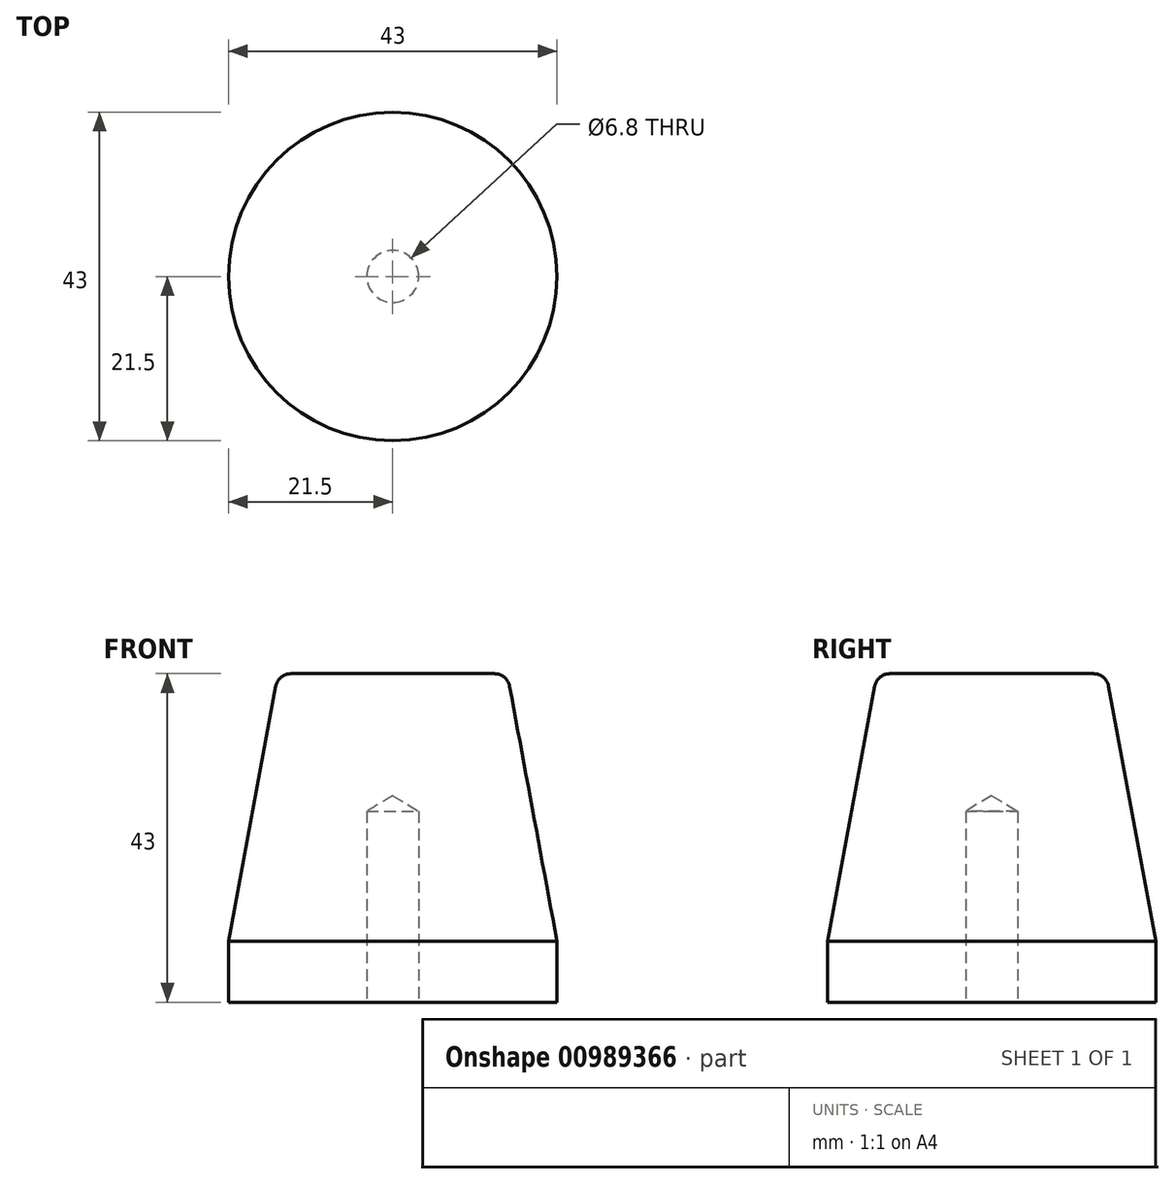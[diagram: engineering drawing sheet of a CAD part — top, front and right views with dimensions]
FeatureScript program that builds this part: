
annotation { "Feature Type Name" : "Feature", "Feature Type Description" : "" }
export const myFeature = defineFeature(function(context is Context, id is Id, definition is map)
    precondition{}
    {
        {
            var Q0;
            Q0=qCreatedBy(makeId("Top.planeOp"),FACE);
            var sketch = newSketch(context, id + "F0", { "sketchPlane" : qUnion([Q0])});
            skCircle(sketch, "E0", {"center": v(0, 0) * mm, "radius": 21.5 * mm});
            skSolve(sketch);
        }
        {
            var Q0;
            Q0 = qSketchRegion(id + "F0", true);
            extrude(context, id + "F1", {"entities" : qUnion([Q0]), "depth" : 8 * mm, "offsetDistance" : 25 * mm});
        }
        {
            var Q0;
            Q0=qCreatedBy(makeId("Top.planeOp"),FACE);
            cPlane(context, id + "F2", {"entities" : qUnion([Q0]), "cplaneType" : CPlaneType.OFFSET, "offset" : 43 * mm, "width" : 150 * mm, "height" : 150 * mm});
        }
        {
            var Q0;
            Q0=qCreatedBy(id+"F2.planeOp",FACE);
            var sketch = newSketch(context, id + "F3", { "sketchPlane" : qUnion([Q0])});
            skCircle(sketch, "E1", {"center": v(0, 0) * mm, "radius": 15 * mm});
            skSolve(sketch);
        }
        {
            var Q1;
            Q1=makeQuery(id+"F3.imprint","IMPRINT",FACE,{"disambiguationData":[TD([[makeQuery(id+"F3.imprint","IMPRINT",EDGE,{"derivedFrom":sQuery(id+"F3.wireOp",EDGE,"E1")}),1.0]])]});
            var Q2;
            Q2=makeQuery(id+"F1.opExtrude","CAP_FACE",FACE,{"disambiguationData":[OSD([sQuery(id+"F0.wireOp",EDGE,"E0")])],"isStart":false});
            loft(context, id + "F4", {"operationType" : NewBodyOperationType.ADD, "sheetProfilesArray" : [{ "sheetProfileEntities" : qUnion([Q1]) }, { "sheetProfileEntities" : qUnion([Q2]) }]});
        }
        {
            var Q0;
            Q0=makeQuery(id+"F1.opExtrude","CAP_FACE",FACE,{"disambiguationData":[OSD([sQuery(id+"F0.wireOp",EDGE,"E0")])],"isStart":true});
            var sketch = newSketch(context, id + "F5", { "sketchPlane" : qUnion([Q0])});
            skPoint(sketch, "E2", {"position": v(0, 0) * mm});
            skSolve(sketch);
        }
        {
            var Q0;
            Q0=sQuery(id+"F5.wireOp",VERTEX,"E2");
            var Q1;
            Q1=makeQuery(id+"F1.opExtrude","SWEPT_BODY",BODY,{"disambiguationData":[OSD([sQuery(id+"F0.wireOp",EDGE,"E0")])]});
            hole(context, id + "F6", {"style" : HoleStyle.SIMPLE, "endStyle" : HoleEndStyle.BLIND, "standardTappedOrClearance" : lookupTablePath({ "standard" : "ISO", "engagement" : "75%", "pitch" : "1.25 mm", "size" : "M8", "type" : "Tapped" }), "standardBlindInLast" : lookupTablePath({ "standard" : "ISO", "fit" : "Normal", "engagement" : "75%", "pitch" : "1.25 mm", "size" : "M8", "type" : "Clearance & tapped" }), "holeDiameter" : 6.8 * mm, "majorDiameter" : 8 * mm, "showTappedDepth" : true, "holeDepth" : 25 * mm, "isTappedThrough" : true, "tappedDepth" : 21.25 * mm, "tapClearance" : 3, "startFromSketch" : true, "locations" : qUnion([Q0]), "scope" : qUnion([Q1])});
        }
        {
            var Q0;
            Q0=makeQuery(id+"F4.opLoft","MID_CAP_EDGE",EDGE,{"disambiguationData":[OSD([sQuery(id+"F3.wireOp",EDGE,"E1")])],"capPos":0.0});
            fillet(context, id + "F7", {"entities" : qUnion([Q0]), "radius" : 2 * mm, "tangentPropagation" : true, "allowEdgeOverflow" : false});
        }
    });
